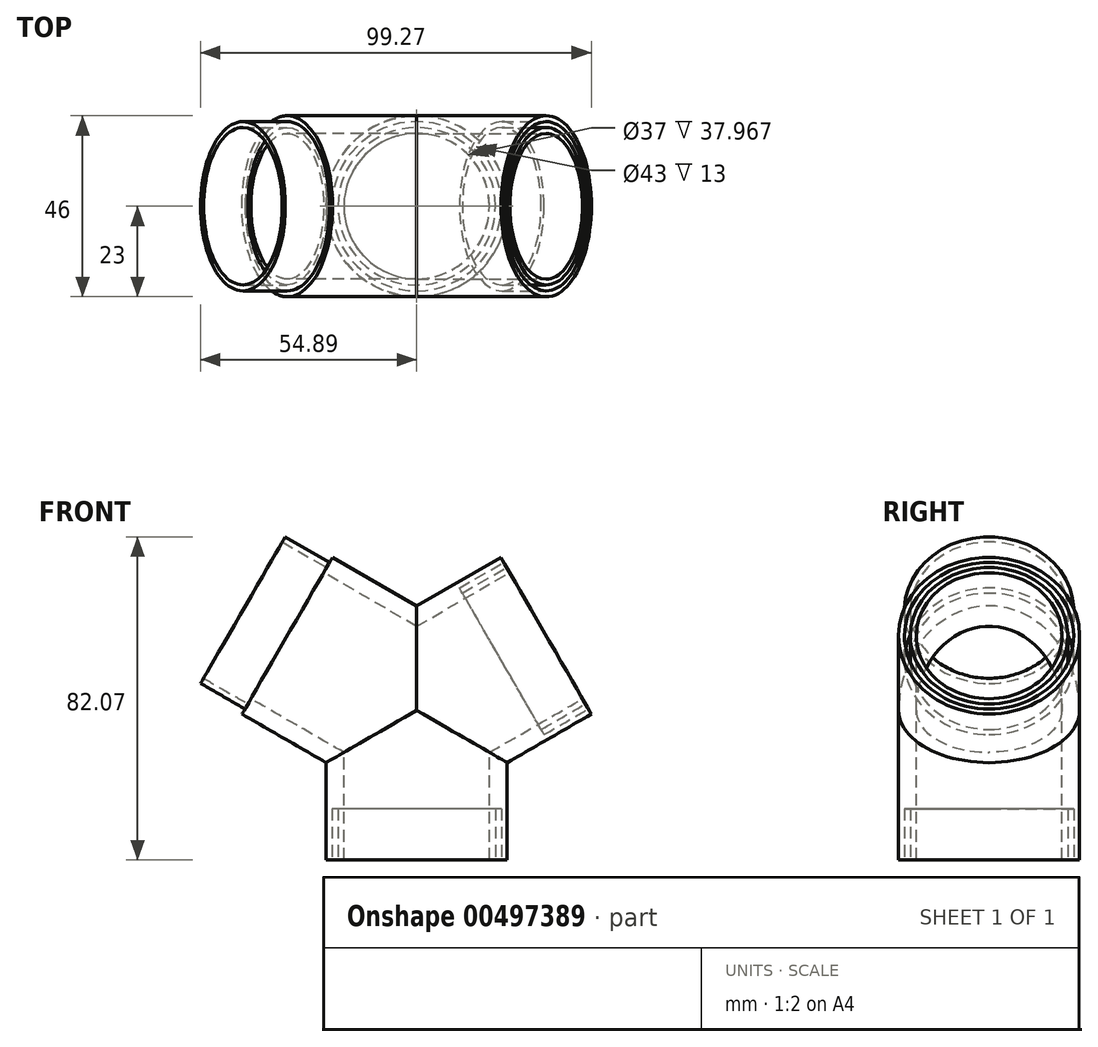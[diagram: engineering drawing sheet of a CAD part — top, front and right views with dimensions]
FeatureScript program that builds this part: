
annotation { "Feature Type Name" : "Feature", "Feature Type Description" : "" }
export const myFeature = defineFeature(function(context is Context, id is Id, definition is map)
    precondition{}
    {
        {
            var Q0;
            Q0=qCreatedBy(makeId("Front.planeOp"),FACE);
            var sketch = newSketch(context, id + "F0", { "sketchPlane" : qUnion([Q0])});
            skLineSegment(sketch, "E0", {"start": v(0, 0) * mm, "end": v(0, 37.97) * mm});
            skLineSegment(sketch, "E1", {"start": v(0, 37.97) * mm, "end": v(32.88, 56.95) * mm});
            skSolve(sketch);
        }
        {
            var Q0;
            Q0=qCreatedBy(makeId("Top.planeOp"),FACE);
            var sketch = newSketch(context, id + "F1", { "sketchPlane" : qUnion([Q0])});
            skPoint(sketch, "E2.0", {"position": v(0, 0) * mm});
            skCircle(sketch, "E3", {"center": v(0, 0) * mm, "radius": 23 * mm});
            skCircle(sketch, "E4.0", {"center": v(0, 0) * mm, "radius": 21.5 * mm});
            skCircle(sketch, "E5.0", {"center": v(0, 0) * mm, "radius": 20 * mm});
            skCircle(sketch, "E6.0", {"center": v(0, 0) * mm, "radius": 18.5 * mm});
            skSolve(sketch);
        }
        {
            var Q0;
            Q0=makeQuery(id+"F1.imprint","IMPRINT",FACE,{"disambiguationData":[TD([[makeQuery(id+"F1.imprint","IMPRINT",EDGE,{"derivedFrom":sQuery(id+"F1.wireOp",EDGE,"E3")}),1.0]])]});
            var Q1;
            Q1=makeQuery(id+"F1.imprint","IMPRINT",FACE,{"disambiguationData":[TD([[makeQuery(id+"F1.imprint","IMPRINT",EDGE,{"derivedFrom":sQuery(id+"F1.wireOp",EDGE,"E5.0")}),1.0]])]});
            var Q2;
            Q2=makeQuery(id+"F1.imprint","IMPRINT",FACE,{"disambiguationData":[TD([[makeQuery(id+"F1.imprint","IMPRINT",EDGE,{"derivedFrom":sQuery(id+"F1.wireOp",EDGE,"E4.0")}),1.0]])]});
            var Q3;
            Q3=sQuery(id+"F0.wireOp",EDGE,"E0");
            var Q4;
            Q4=sQuery(id+"F0.wireOp",EDGE,"E1");
            sweep(context, id + "F2", {"profiles" : qUnion([Q0, Q1, Q2]), "path" : qUnion([Q3, Q4])});
        }
        {
            var Q0;
            Q0=makeQuery(id+"F2.opSweep","CAP_FACE",FACE,{"disambiguationData":[OSD([sQuery(id+"F0.wireOp",VERTEX,"E1.end"),sQuery(id+"F1.wireOp",EDGE,"E3"),sQuery(id+"F1.wireOp",EDGE,"E6.0")])],"isStart":false});
            var sketch = newSketch(context, id + "F3", { "sketchPlane" : qUnion([Q0])});
            skCircle(sketch, "E7.0", {"center": v(0, 32.88) * mm, "radius": 23 * mm});
            skCircle(sketch, "E8.0", {"center": v(0, 32.88) * mm, "radius": 18.5 * mm});
            skCircle(sketch, "E9", {"center": v(0, 32.88) * mm, "radius": 21.5 * mm});
            skCircle(sketch, "E10", {"center": v(0, 32.88) * mm, "radius": 20 * mm});
            skSolve(sketch);
        }
        {
            var Q0;
            Q0=makeQuery(id+"F3.imprint","IMPRINT",FACE,{"disambiguationData":[TD([[makeQuery(id+"F3.imprint","IMPRINT",EDGE,{"derivedFrom":sQuery(id+"F3.wireOp",EDGE,"E9")}),1.0]])]});
            extrude(context, id + "F4", {"entities" : qUnion([Q0]), "operationType" : NewBodyOperationType.REMOVE, "oppositeDirection" : true, "depth" : 13 * mm, "offsetDistance" : 25 * mm});
        }
        {
            var Q0;
            Q0=makeQuery(id+"F1.imprint","IMPRINT",FACE,{"disambiguationData":[TD([[makeQuery(id+"F1.imprint","IMPRINT",EDGE,{"derivedFrom":sQuery(id+"F1.wireOp",EDGE,"E4.0")}),1.0]])]});
            extrude(context, id + "F5", {"entities" : qUnion([Q0]), "operationType" : NewBodyOperationType.REMOVE, "depth" : 13 * mm, "offsetDistance" : 25.4 * mm});
        }
        {
            var Q0;
            Q0=makeQuery(id+"F2.opSweep","SWEPT_BODY",BODY,{"disambiguationData":[OSD([sQuery(id+"F0.wireOp",EDGE,"E1"),sQuery(id+"F1.wireOp",EDGE,"E3"),sQuery(id+"F1.wireOp",EDGE,"E6.0")])]});
            var Q1;
            Q1=qCreatedBy(makeId("Right.planeOp"),FACE);
            mirror(context, id + "F6", {"operationType" : NewBodyOperationType.ADD, "entities" : qUnion([Q0]), "mirrorPlane" : qUnion([Q1])});
        }
        {
            var Q0;
            Q0=makeQuery(id+"F3.imprint","IMPRINT",FACE,{"disambiguationData":[TD([[makeQuery(id+"F3.imprint","IMPRINT",EDGE,{"derivedFrom":sQuery(id+"F3.wireOp",EDGE,"E8.0")}),-1.0]])]});
            extrude(context, id + "F7", {"entities" : qUnion([Q0]), "oppositeDirection" : true, "depth" : 38.1 * mm, "offsetDistance" : 25.4 * mm});
        }
        {
            var Q0;
            Q0=makeQuery(id+"F7.opExtrude","SWEPT_BODY",BODY,{"disambiguationData":[OSD([sQuery(id+"F3.wireOp",EDGE,"E8.0")])]});
            var Q1;
            Q1=qCreatedBy(makeId("Right.planeOp"),FACE);
            mirror(context, id + "F8", {"operationType" : NewBodyOperationType.REMOVE, "entities" : qUnion([Q0]), "mirrorPlane" : qUnion([Q1])});
        }
        {
            var Q0;
            Q0=makeQuery(id+"F3.imprint","IMPRINT",FACE,{"disambiguationData":[TD([[makeQuery(id+"F3.imprint","IMPRINT",EDGE,{"derivedFrom":sQuery(id+"F3.wireOp",EDGE,"E8.0")}),-1.0]])]});
            extrude(context, id + "F9", {"entities" : qUnion([Q0]), "operationType" : NewBodyOperationType.REMOVE, "oppositeDirection" : true, "depth" : 38.1 * mm, "offsetDistance" : 25.4 * mm});
        }
        {
            var Q0;
            Q0=makeQuery(id+"F6.opPattern","COPY",FACE,{"derivedFrom":makeQuery(id+"F4.boolean.opBoolean","COPY",FACE,{"derivedFrom":makeQuery(id+"F4.opExtrude","CAP_FACE",FACE,{"disambiguationData":[OSD([sQuery(id+"F3.wireOp",EDGE,"E9"),sQuery(id+"F3.wireOp",EDGE,"E10")])],"isStart":false})}),"instanceName":"1"});
            var sketch = newSketch(context, id + "F10", { "sketchPlane" : qUnion([Q0])});
            skCircle(sketch, "E11.0", {"center": v(0, 32.88) * mm, "radius": 21.5 * mm});
            skCircle(sketch, "E12.0", {"center": v(0, 32.88) * mm, "radius": 20 * mm});
            skSolve(sketch);
        }
        {
            var Q0;
            Q0=makeQuery(id+"F10.imprint","IMPRINT",FACE,{"disambiguationData":[TD([[makeQuery(id+"F10.imprint","IMPRINT",EDGE,{"derivedFrom":sQuery(id+"F10.wireOp",EDGE,"E11.0")}),-1.0]])]});
            extrude(context, id + "F11", {"entities" : qUnion([Q0]), "operationType" : NewBodyOperationType.ADD, "depth" : 26 * mm, "offsetDistance" : 25 * mm});
        }
    });
